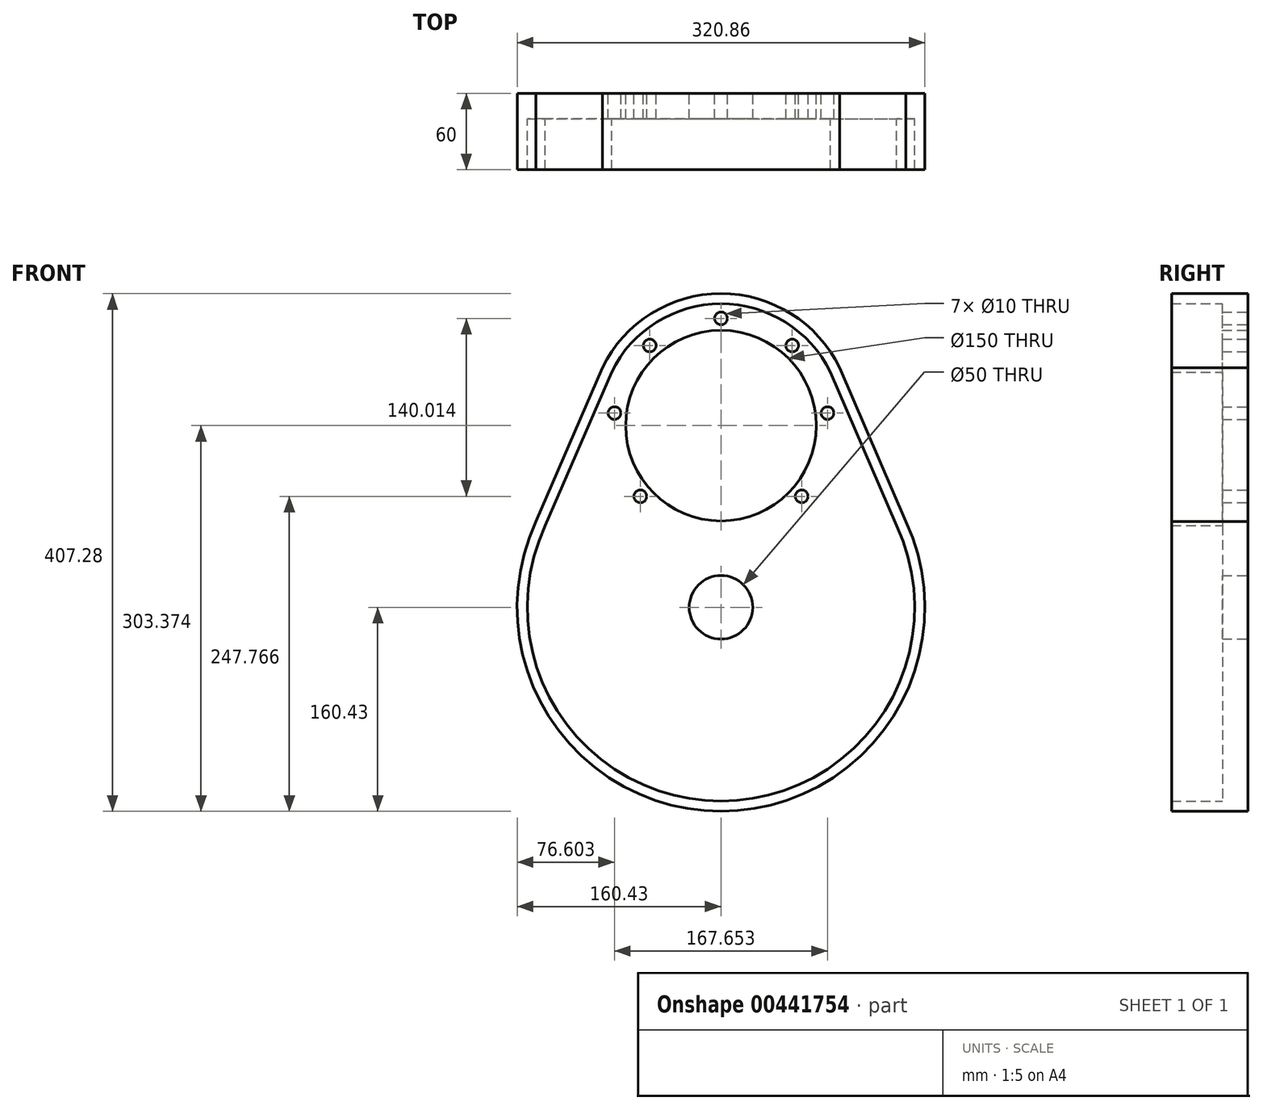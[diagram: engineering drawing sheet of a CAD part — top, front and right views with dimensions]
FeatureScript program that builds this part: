
annotation { "Feature Type Name" : "Feature", "Feature Type Description" : "" }
export const myFeature = defineFeature(function(context is Context, id is Id, definition is map)
    precondition{}
    {
        {
            var Q0;
            Q0=qCreatedBy(makeId("Front.planeOp"),FACE);
            var sketch = newSketch(context, id + "F0", { "sketchPlane" : qUnion([Q0])});
            skCircle(sketch, "E0", {"center": v(0, 0) * mm, "radius": 247.65 * mm, "construction": true});
            skCircle(sketch, "E1", {"center": v(0, 142.94) * mm, "radius": 75 * mm});
            skCircle(sketch, "E2", {"center": v(0, 142.94) * mm, "radius": 95 * mm, "construction": true});
            skCircle(sketch, "E3", {"center": v(0, 142.94) * mm, "radius": 84.4 * mm, "construction": true});
            skCircle(sketch, "E4", {"center": v(0, 227.35) * mm, "radius": 5 * mm});
            skCircle(sketch, "E5", {"center": v(-56.08, 206.03) * mm, "radius": 5 * mm});
            skCircle(sketch, "E6", {"center": v(-83.83, 152.83) * mm, "radius": 5 * mm});
            skCircle(sketch, "E7", {"center": v(-63.5, 87.34) * mm, "radius": 5 * mm});
            skCircle(sketch, "E8.MirrorC", {"center": v(83.83, 152.83) * mm, "radius": 5 * mm});
            skCircle(sketch, "E9.MirrorC", {"center": v(56.08, 206.03) * mm, "radius": 5 * mm});
            skCircle(sketch, "E10.MirrorC", {"center": v(63.5, 87.34) * mm, "radius": 5 * mm});
            skArc(sketch, "E11", {"start": v(93.4, 188.46) * mm, "mid": v(0, 246.85) * mm, "end": v(-93.4, 188.46) * mm});
            skCircle(sketch, "E12", {"center": v(0, 142.94) * mm, "radius": 40 * mm, "construction": true});
            skCircle(sketch, "E13", {"center": v(0, 0) * mm, "radius": 25 * mm});
            skArc(sketch, "E14", {"start": v(-145.52, 67.54) * mm, "mid": v(0, -160.43) * mm, "end": v(145.52, 67.54) * mm});
            skLineSegment(sketch, "E15", {"start": v(-93.4, 188.46) * mm, "end": v(-145.52, 67.54) * mm});
            skLineSegment(sketch, "E16.MirrorCS", {"start": v(93.4, 188.46) * mm, "end": v(145.52, 67.54) * mm});
            skPoint(sketch, "E17.orphan", {"position": v(-149.02, 59.42) * mm});
            skPoint(sketch, "E18.orphan", {"position": v(149.02, 59.42) * mm});
            skLineSegment(sketch, "E19.0", {"start": v(-86.13, 185.12) * mm, "end": v(-138.22, 64.27) * mm});
            skArc(sketch, "E19.1", {"start": v(86.13, 185.12) * mm, "mid": v(0, 238.85) * mm, "end": v(-86.13, 185.12) * mm});
            skLineSegment(sketch, "E19.2", {"start": v(86.13, 185.12) * mm, "end": v(138.22, 64.27) * mm});
            skArc(sketch, "E19.3", {"start": v(-138.22, 64.27) * mm, "mid": v(0, -152.43) * mm, "end": v(138.22, 64.27) * mm});
            skSolve(sketch);
        }
        {
            var Q0;
            Q0=makeQuery(id+"F0.imprint","IMPRINT",FACE,{"disambiguationData":[TD([[makeQuery(id+"F0.imprint","IMPRINT",EDGE,{"derivedFrom":sQuery(id+"F0.wireOp",EDGE,"E1")}),-1.0]])]});
            extrude(context, id + "F1", {"entities" : qUnion([Q0]), "depth" : 20 * mm});
        }
        {
            var Q0;
            Q0=makeQuery(id+"F0.imprint","IMPRINT",FACE,{"disambiguationData":[TD([[makeQuery(id+"F0.imprint","IMPRINT",EDGE,{"derivedFrom":sQuery(id+"F0.wireOp",EDGE,"E11")}),1.0]])]});
            extrude(context, id + "F2", {"entities" : qUnion([Q0]), "operationType" : NewBodyOperationType.ADD, "depth" : 60 * mm});
        }
    });
